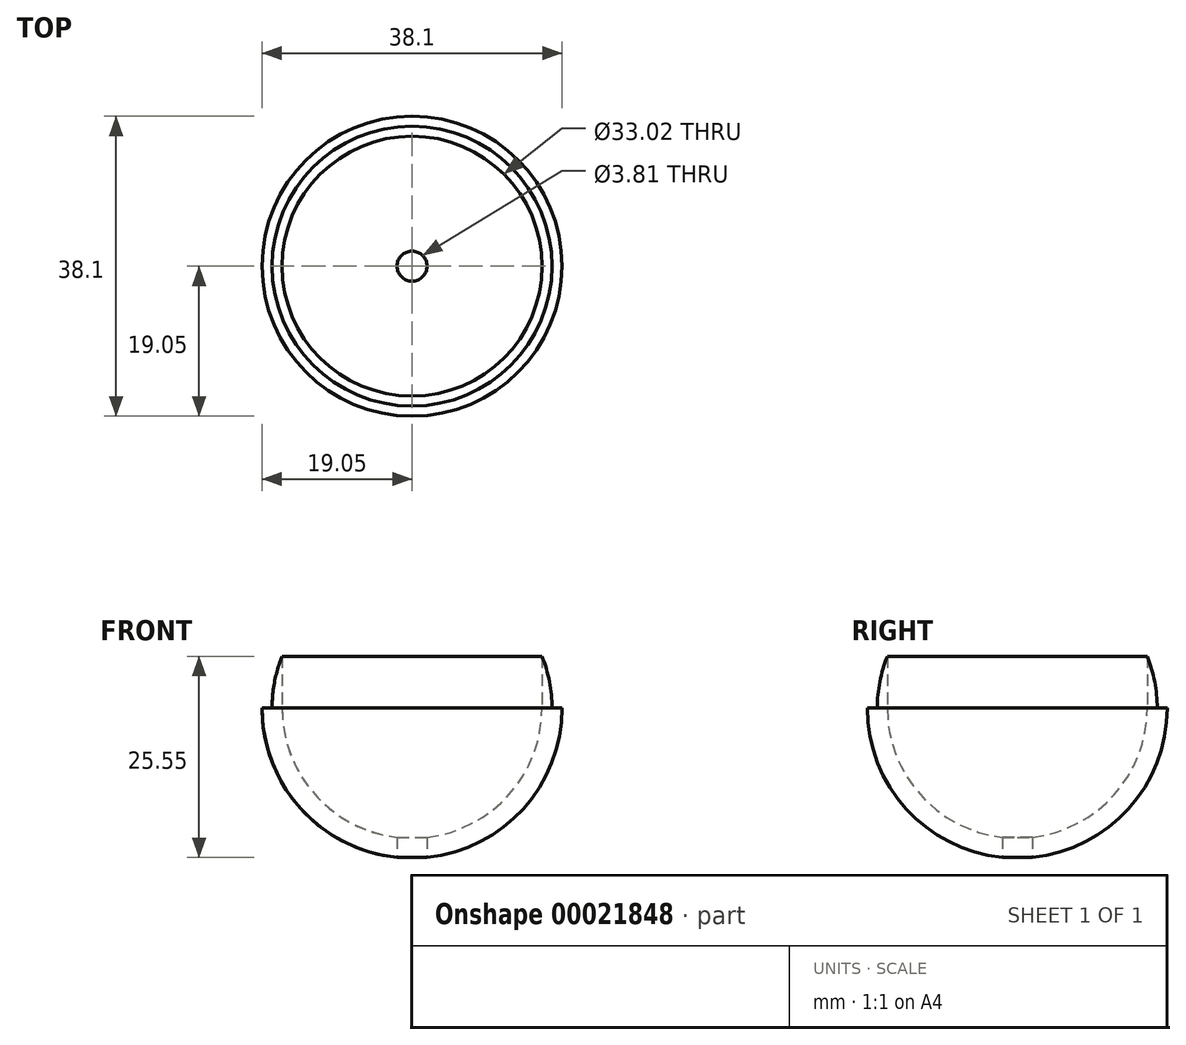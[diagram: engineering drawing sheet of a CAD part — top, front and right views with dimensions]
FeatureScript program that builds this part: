
annotation { "Feature Type Name" : "Feature", "Feature Type Description" : "" }
export const myFeature = defineFeature(function(context is Context, id is Id, definition is map)
    precondition{}
    {
        {
            var Q0;
            Q0=qCreatedBy(makeId("Front.planeOp"),FACE);
            var sketch = newSketch(context, id + "F0", { "sketchPlane" : qUnion([Q0])});
            skArc(sketch, "E0", {"start": v(-19.05, 0) * mm, "mid": v(0, -19.05) * mm, "end": v(19.05, 0) * mm});
            skLineSegment(sketch, "E1", {"start": v(0, 0) * mm, "end": v(0, 3.18) * mm});
            skLineSegment(sketch, "E2", {"start": v(0, -23.25) * mm, "end": v(0, 9.84) * mm});
            skLineSegment(sketch, "E3", {"start": v(-19.05, 0) * mm, "end": v(-17.78, 0) * mm});
            skLineSegment(sketch, "E4", {"start": v(19.05, 0) * mm, "end": v(17.78, 0) * mm});
            skArc(sketch, "E5", {"start": v(17.78, 0) * mm, "mid": v(0, 17.78) * mm, "end": v(-17.78, 0) * mm});
            skLineSegment(sketch, "E6", {"start": v(-16.51, 0) * mm, "end": v(-16.51, 6.6) * mm});
            skLineSegment(sketch, "E7.MirrorCS", {"start": v(16.51, 0) * mm, "end": v(16.51, 6.6) * mm});
            skArc(sketch, "E8", {"start": v(-16.51, 0) * mm, "mid": v(0, -16.51) * mm, "end": v(16.51, 0) * mm});
            skLineSegment(sketch, "E9", {"start": v(0, -15.84) * mm, "end": v(-1.9, -15.84) * mm});
            skLineSegment(sketch, "E10", {"start": v(-1.9, -15.84) * mm, "end": v(-1.9, -18.95) * mm});
            skSolve(sketch);
        }
        {
            var Q0;
            {var subQ7=sQuery(id+"F0.wireOp",EDGE,"E3");Q0=makeQuery(id+"F0.imprint","IMPRINT",FACE,{"disambiguationData":[TD([[makeQuery(id+"F0.imprint","IMPRINT",EDGE,{"derivedFrom":subQ7}),-1.0]])]});}
            var Q1;
            Q1=sQuery(id+"F0.wireOp",EDGE,"E2");
            revolve(context, id + "F1", {"entities" : qUnion([Q0]), "axis" : qUnion([Q1]), "revolveType" : RevolveType.FULL});
        }
    });
